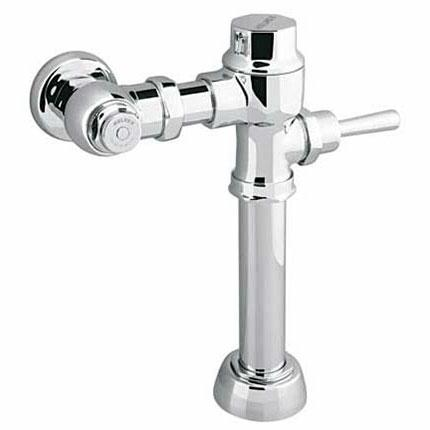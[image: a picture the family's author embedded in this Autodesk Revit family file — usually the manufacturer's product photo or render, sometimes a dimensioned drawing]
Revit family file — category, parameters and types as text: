
# Revit family: 110-38-3.5
name_source: partatom
category: Aparatos sanitarios
units: mm (PartAtom-declared; Revit-internal decimal feet)

## family parameters
Compartido = Sí
Corte con vacíos al cargar = No
Cota de conector redondo = Diámetro de uso
Número OmniClass = 23.45.00.00
Punto de cálculo de habitación = No
Se basa en plano de trabajo = No
Siempre vertical = Sí
Tipo de pieza = Normal
Título OmniClass = Sanitary, Laundry, and Cleaning Equipment

## types (1)
- 110-38-3.5
    Chrome = Brass Chromed
    Comentarios de tipo = Fluxómetros
    Conexión AF = Sí
    Connection = tubo Ø 25,4mm
    Descripción = Fluxómetro para W. C. de Manija
    Documentation = https://www.helvex.com.mx
    Elevación por defecto = 0"
    Fabricante = HELVEX
    Features = Instalación izquierda o derecha
    Imagen de tipo = 110-38-3.5.jpg
    Instructive = https://www.helvex.com.mx
    Max. Working Pressure = 85.3 psi
    Min. Working Pressure = 28.4 psi
    Modelo = 110-38-3.5
    Note = La tubería de alimentación debe tener un Ø 32mm
mínimo y debe conectarse una reducción de
campana de 32mm - 25mm a la llave de retención.
    URL = https://www.helvex.com.mx

## geometry (parser evidence)
native form markers: Sweep x3
no freeform markers — native parametric forms only
